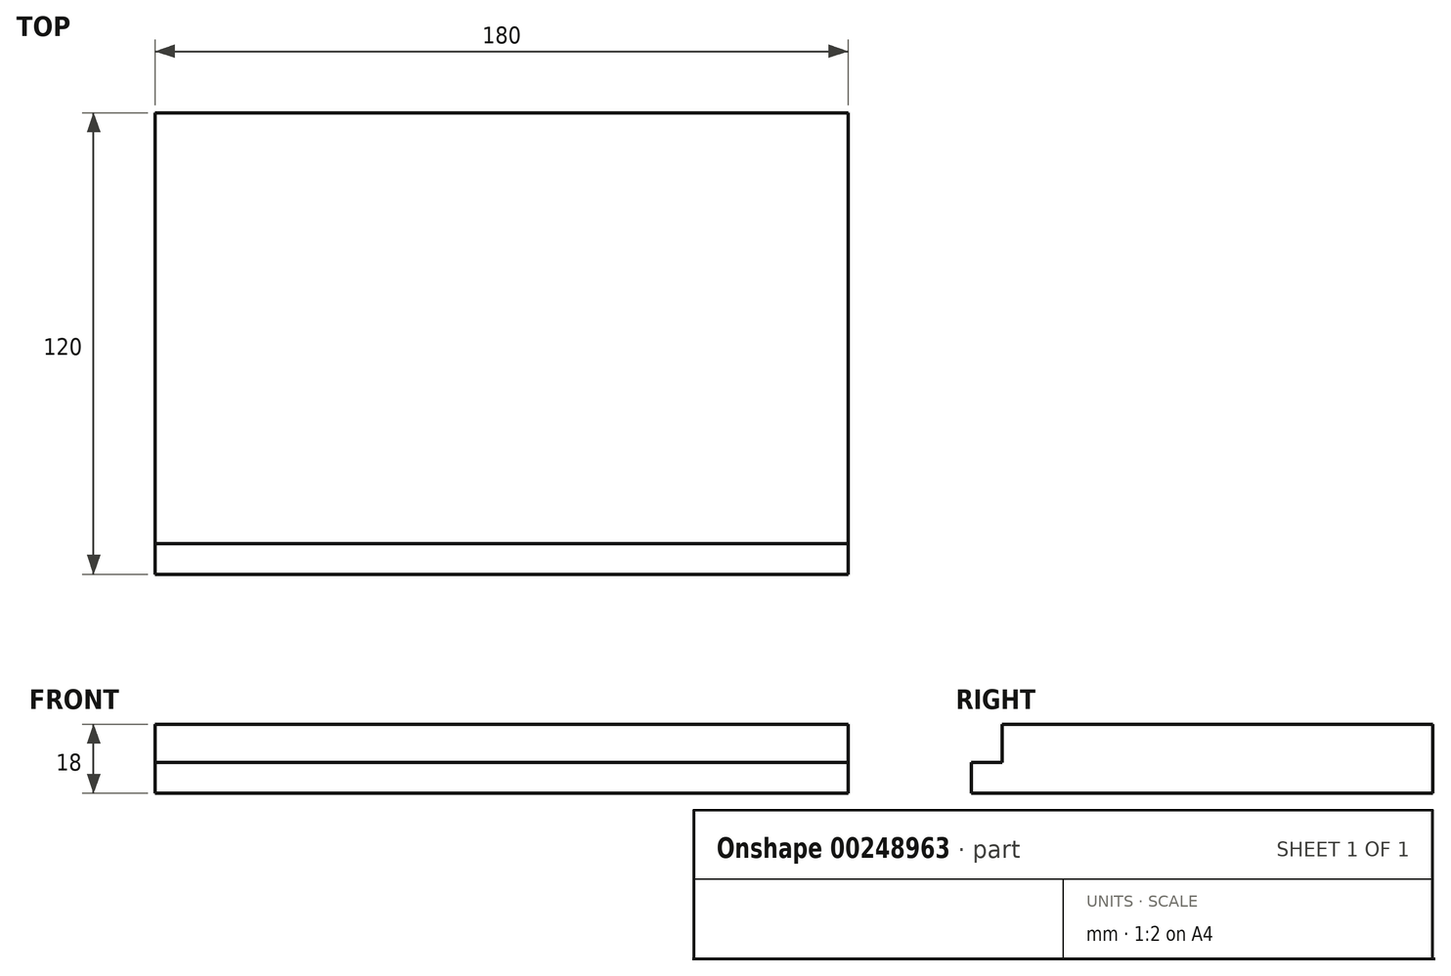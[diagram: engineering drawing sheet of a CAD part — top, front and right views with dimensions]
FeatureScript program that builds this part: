
annotation { "Feature Type Name" : "Feature", "Feature Type Description" : "" }
export const myFeature = defineFeature(function(context is Context, id is Id, definition is map)
    precondition{}
    {
        {
            var Q0;
            Q0=qCreatedBy(makeId("Top.planeOp"),FACE);
            var sketch = newSketch(context, id + "F0", { "sketchPlane" : qUnion([Q0])});
            skLineSegment(sketch, "E0.bottom", {"start": v(-90, -60) * mm, "end": v(90, -60) * mm});
            skLineSegment(sketch, "E0.top", {"start": v(-90, 60) * mm, "end": v(90, 60) * mm});
            skLineSegment(sketch, "E0.left", {"start": v(-90, 60) * mm, "end": v(-90, -60) * mm});
            skLineSegment(sketch, "E0.right", {"start": v(90, 60) * mm, "end": v(90, -60) * mm});
            skPoint(sketch, "E1", {"position": v(90, 0) * mm});
            skPoint(sketch, "E2", {"position": v(0, 60) * mm});
            skSolve(sketch);
        }
        {
            var Q0;
            Q0=qSketchRegion(id+"F0",true);
            extrude(context, id + "F1", {"entities" : qUnion([Q0]), "depth" : 18 * mm});
        }
        {
            var Q0;
            Q0=makeQuery(id+"F1.opExtrude","SWEPT_FACE",FACE,{"disambiguationData":[OSD([sQuery(id+"F0.wireOp",EDGE,"E0.bottom")])]});
            var sketch = newSketch(context, id + "F2", { "sketchPlane" : qUnion([Q0])});
            skLineSegment(sketch, "E3.0", {"start": v(-90, 18) * mm, "end": v(90, 18) * mm});
            skLineSegment(sketch, "E4", {"start": v(-90, 18) * mm, "end": v(-90, 8) * mm});
            skLineSegment(sketch, "E5", {"start": v(-90, 8) * mm, "end": v(90, 8) * mm});
            skLineSegment(sketch, "E6", {"start": v(90, 8) * mm, "end": v(90, 18) * mm});
            skSolve(sketch);
        }
        {
            var Q0;
            Q0=qSketchRegion(id+"F2",true);
            extrude(context, id + "F3", {"entities" : qUnion([Q0]), "operationType" : NewBodyOperationType.REMOVE, "oppositeDirection" : true, "depth" : 8 * mm});
        }
    });
